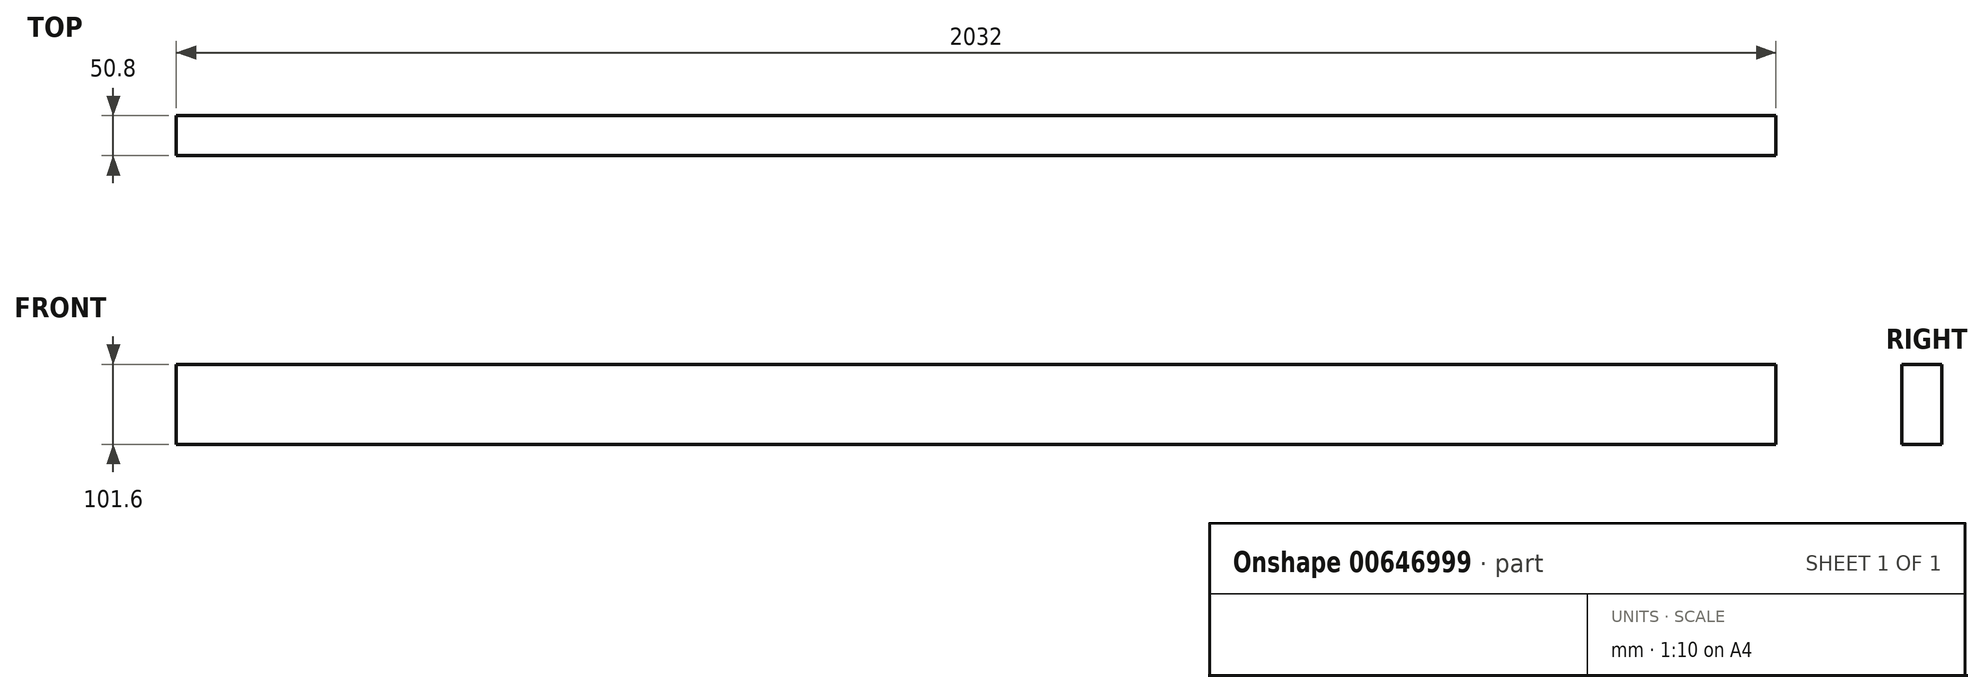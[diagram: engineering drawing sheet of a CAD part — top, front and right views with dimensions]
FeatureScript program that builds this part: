
annotation { "Feature Type Name" : "Feature", "Feature Type Description" : "" }
export const myFeature = defineFeature(function(context is Context, id is Id, definition is map)
    precondition{}
    {
        {
            var Q0;
            Q0=qCreatedBy(makeId("Front.planeOp"),FACE);
            var sketch = newSketch(context, id + "F0", { "sketchPlane" : qUnion([Q0])});
            skLineSegment(sketch, "E0.bottom", {"start": v(-172.97, 77.1) * mm, "end": v(1859.03, 77.1) * mm});
            skLineSegment(sketch, "E0.top", {"start": v(-172.97, -24.5) * mm, "end": v(1859.03, -24.5) * mm});
            skLineSegment(sketch, "E0.left", {"start": v(-172.97, 77.1) * mm, "end": v(-172.97, -24.5) * mm});
            skLineSegment(sketch, "E0.right", {"start": v(1859.03, 77.1) * mm, "end": v(1859.03, -24.5) * mm});
            skSolve(sketch);
        }
        {
            var Q0;
            Q0 = qSketchRegion(id + "F0", true);
            extrude(context, id + "F1", {"entities" : qUnion([Q0]), "depth" : 50.8 * mm, "offsetDistance" : 25.4 * mm});
        }
    });
